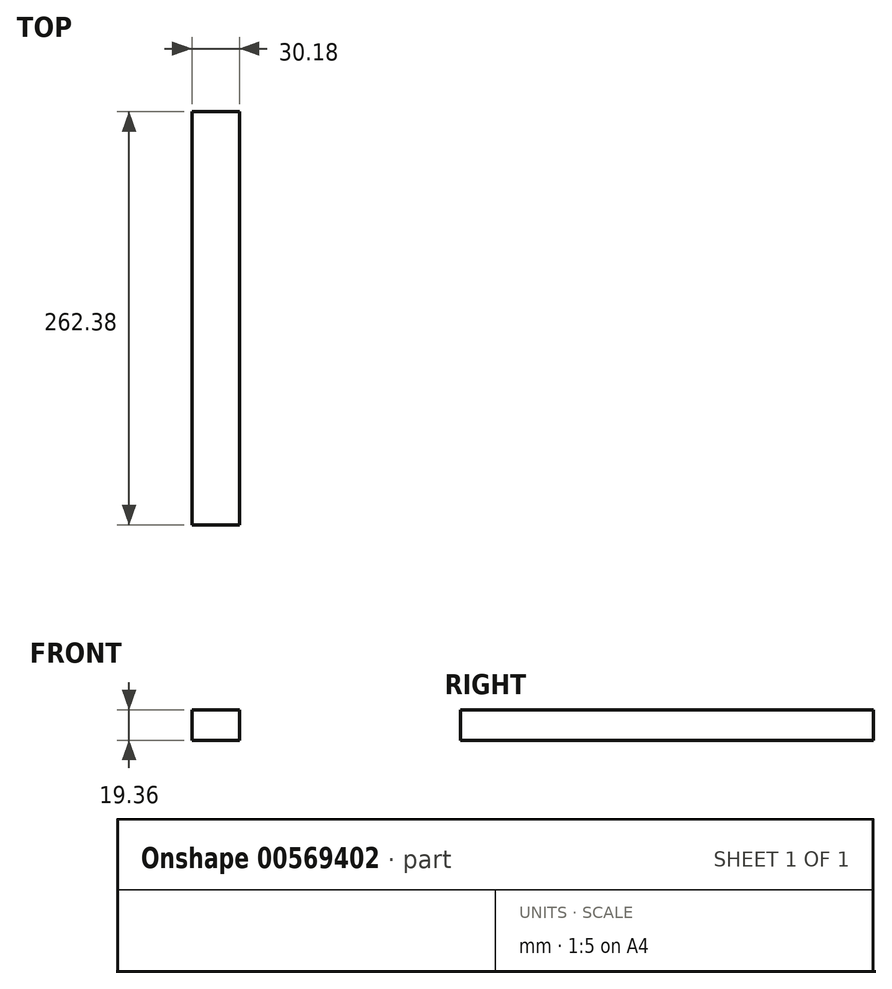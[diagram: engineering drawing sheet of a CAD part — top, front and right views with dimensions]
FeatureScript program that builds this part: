
annotation { "Feature Type Name" : "Feature", "Feature Type Description" : "" }
export const myFeature = defineFeature(function(context is Context, id is Id, definition is map)
    precondition{}
    {
        {
            var Q0;
            Q0=qCreatedBy(makeId("Front.planeOp"),FACE);
            var sketch = newSketch(context, id + "F0", { "sketchPlane" : qUnion([Q0])});
            skLineSegment(sketch, "E0.bottom", {"start": v(-121.4, 52.79) * mm, "end": v(-91.23, 52.79) * mm});
            skLineSegment(sketch, "E0.top", {"start": v(-121.4, 33.43) * mm, "end": v(-91.23, 33.43) * mm});
            skLineSegment(sketch, "E0.left", {"start": v(-121.4, 52.79) * mm, "end": v(-121.4, 33.43) * mm});
            skLineSegment(sketch, "E0.right", {"start": v(-91.23, 52.79) * mm, "end": v(-91.23, 33.43) * mm});
            skSolve(sketch);
        }
        {
            var Q0;
            Q0=makeQuery(id+"F0.imprint","IMPRINT",FACE,{"disambiguationData":[TD([[makeQuery(id+"F0.imprint","IMPRINT",EDGE,{"derivedFrom":sQuery(id+"F0.wireOp",EDGE,"E0.bottom")}),-1.0]])]});
            extrude(context, id + "F1", {"entities" : qUnion([Q0]), "depth" : 262.38 * mm, "offsetDistance" : 25.4 * mm});
        }
    });
